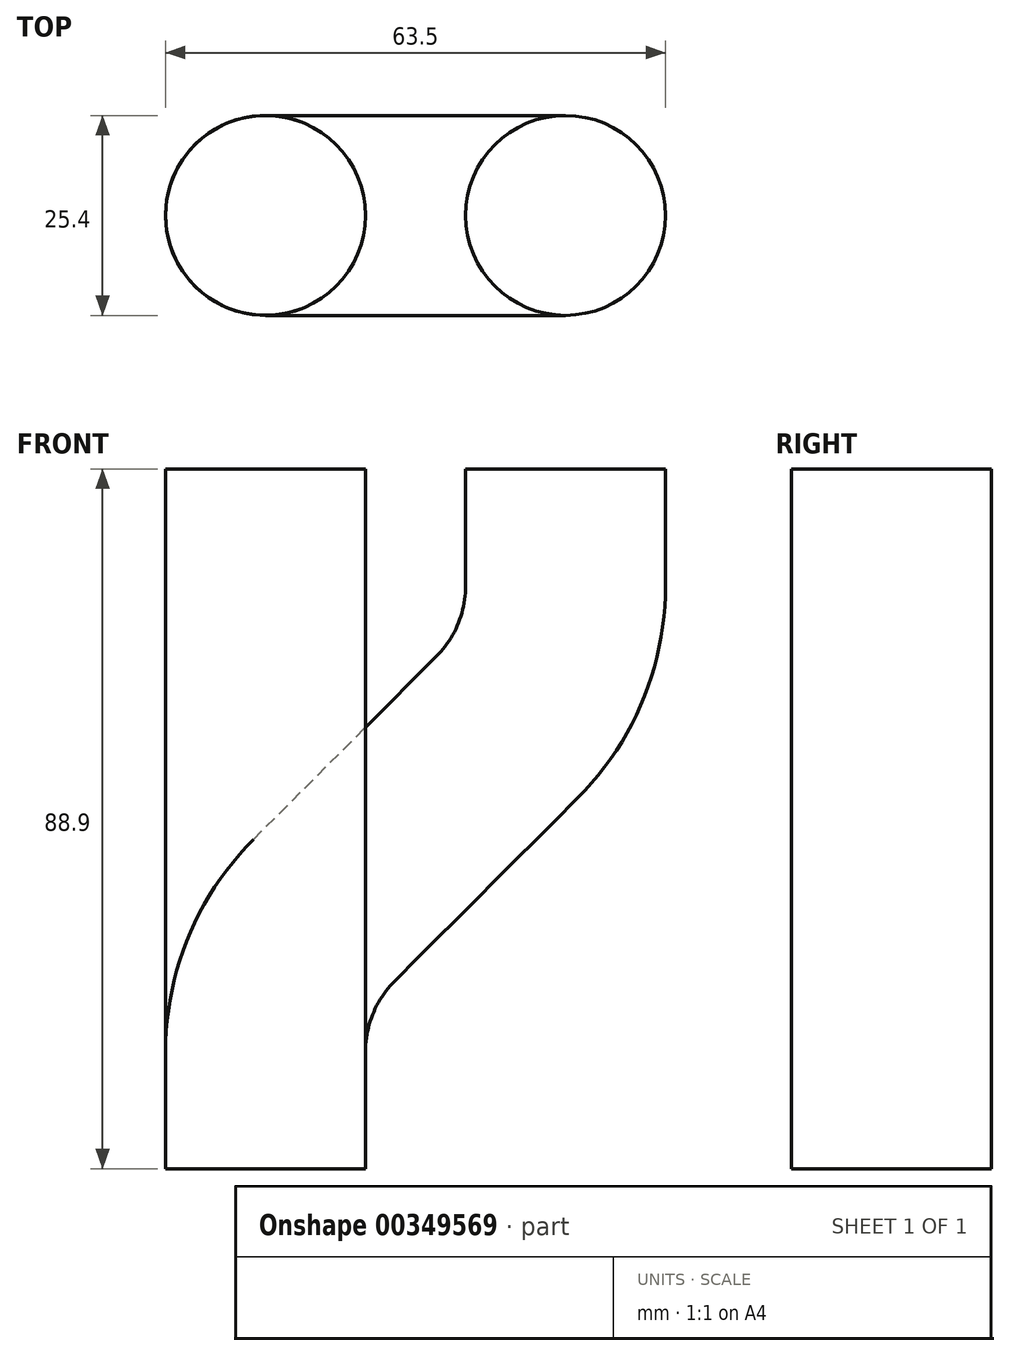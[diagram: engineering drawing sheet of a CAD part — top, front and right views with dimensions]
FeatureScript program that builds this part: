
annotation { "Feature Type Name" : "Feature", "Feature Type Description" : "" }
export const myFeature = defineFeature(function(context is Context, id is Id, definition is map)
    precondition{}
    {
        {
            var Q0;
            Q0=qCreatedBy(makeId("Front.planeOp"),FACE);
            var sketch = newSketch(context, id + "F0", { "sketchPlane" : qUnion([Q0])});
            skLineSegment(sketch, "E0", {"start": v(0, 0) * mm, "end": v(0, 14.88) * mm});
            skLineSegment(sketch, "E1", {"start": v(7.44, 32.84) * mm, "end": v(30.66, 56.06) * mm});
            skLineSegment(sketch, "E2", {"start": v(38.1, 74.02) * mm, "end": v(38.1, 88.9) * mm});
            skPoint(sketch, "E3.visualSharp", {"position": v(0, 25.4) * mm});
            skArc(sketch, "E3.filletArc", {"start": v(7.44, 32.84) * mm, "mid": v(1.93, 24.6) * mm, "end": v(0, 14.88) * mm});
            skPoint(sketch, "E4.visualSharp", {"position": v(38.1, 63.5) * mm});
            skArc(sketch, "E4.filletArc", {"start": v(30.66, 56.06) * mm, "mid": v(36.17, 64.3) * mm, "end": v(38.1, 74.02) * mm});
            skSolve(sketch);
        }
        {
            var Q0;
            Q0=qCreatedBy(makeId("Top.planeOp"),FACE);
            var sketch = newSketch(context, id + "F1", { "sketchPlane" : qUnion([Q0])});
            skCircle(sketch, "E5", {"center": v(0, 0) * mm, "radius": 12.7 * mm});
            skSolve(sketch);
        }
        {
            var Q0;
            Q0=makeQuery(id+"F1.imprint","IMPRINT",FACE,{"disambiguationData":[TD([[makeQuery(id+"F1.imprint","IMPRINT",EDGE,{"derivedFrom":sQuery(id+"F1.wireOp",EDGE,"E5")}),1.0]])]});
            var Q1;
            Q1=sQuery(id+"F1.wireOp",EDGE,"E5");
            var Q2;
            Q2 = qBodyType(qCreatedBy(id + "F0" ,EDGE), BodyType.WIRE);
            sweep(context, id + "F2", {"bodyType" : ToolBodyType.SURFACE, "profiles" : qUnion([Q0]), "surfaceProfiles" : qUnion([Q1]), "path" : qUnion([Q2])});
        }
        {
            var Q0;
            Q0 = qBodyType(qCreatedBy(id + "F1" ,EDGE), BodyType.WIRE);
            extrude(context, id + "F3", {"bodyType" : ToolBodyType.SURFACE, "surfaceEntities" : qUnion([Q0]), "depth" : 88.9 * mm});
        }
    });
